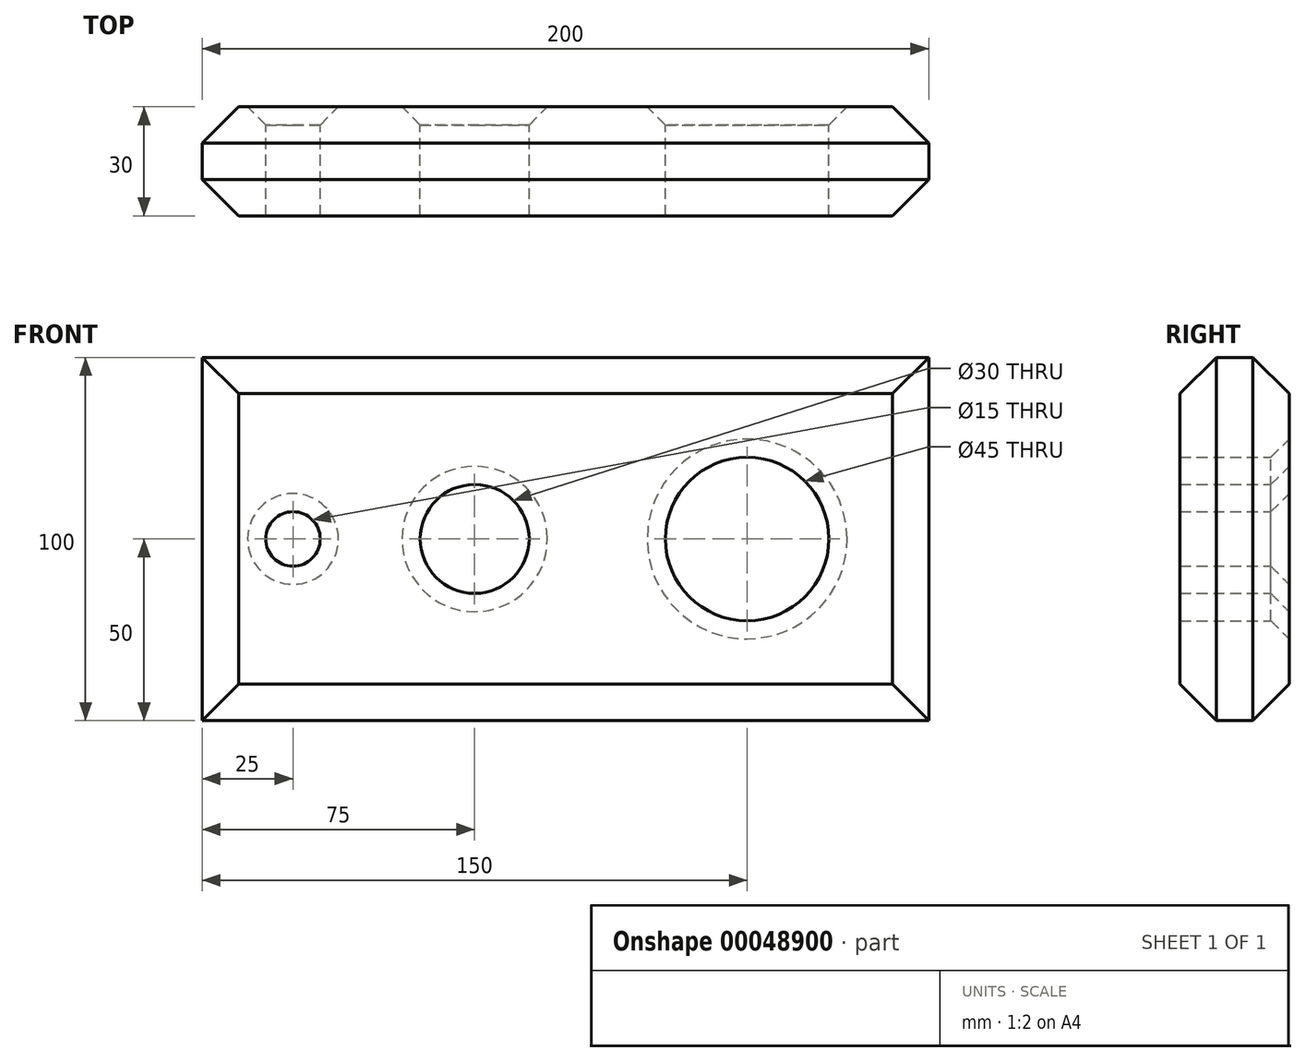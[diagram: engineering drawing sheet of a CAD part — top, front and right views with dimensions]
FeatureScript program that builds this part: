
annotation { "Feature Type Name" : "Feature", "Feature Type Description" : "" }
export const myFeature = defineFeature(function(context is Context, id is Id, definition is map)
    precondition{}
    {
        {
            var Q0;
            Q0=qCreatedBy(makeId("Front.planeOp"),FACE);
            var sketch = newSketch(context, id + "F0", { "sketchPlane" : qUnion([Q0])});
            skLineSegment(sketch, "E0.rect.bottom", {"start": v(100, 50) * mm, "end": v(-100, 50) * mm});
            skLineSegment(sketch, "E0.rect.top", {"start": v(100, -50) * mm, "end": v(-100, -50) * mm});
            skLineSegment(sketch, "E0.rect.left", {"start": v(100, 50) * mm, "end": v(100, -50) * mm});
            skLineSegment(sketch, "E0.rect.right", {"start": v(-100, 50) * mm, "end": v(-100, -50) * mm});
            skPoint(sketch, "E0.rect.middle", {"position": v(0, 0) * mm});
            skLineSegment(sketch, "E1", {"start": v(-75, 50) * mm, "end": v(-75, -50) * mm, "construction": true});
            skLineSegment(sketch, "E2", {"start": v(-25, 50) * mm, "end": v(-25, -50) * mm, "construction": true});
            skLineSegment(sketch, "E3", {"start": v(50, 50) * mm, "end": v(50, -50) * mm, "construction": true});
            skLineSegment(sketch, "E4", {"start": v(-100, 0) * mm, "end": v(100, 0) * mm, "construction": true});
            skCircle(sketch, "E5", {"center": v(-75, 0) * mm, "radius": 7.5 * mm});
            skCircle(sketch, "E6", {"center": v(-25, 0) * mm, "radius": 15 * mm});
            skCircle(sketch, "E7", {"center": v(50, 0) * mm, "radius": 22.5 * mm});
            skSolve(sketch);
        }
        {
            var Q0;
            Q0=makeQuery(id+"F0.imprint","IMPRINT",FACE,{"disambiguationData":[TD([[makeQuery(id+"F0.imprint","IMPRINT",EDGE,{"derivedFrom":sQuery(id+"F0.wireOp",EDGE,"E0.rect.bottom")}),1.0]])]});
            extrude(context, id + "F1", {"entities" : qUnion([Q0]), "depth" : 30 * mm});
        }
        {
            var Q0;
            Q0=makeQuery(id+"F1.opExtrude","CAP_EDGE",EDGE,{"disambiguationData":[OSD([sQuery(id+"F0.wireOp",EDGE,"E5")])],"isStart":true});
            var Q1;
            Q1=makeQuery(id+"F1.opExtrude","CAP_EDGE",EDGE,{"disambiguationData":[OSD([sQuery(id+"F0.wireOp",EDGE,"E6")])],"isStart":true});
            var Q2;
            Q2=makeQuery(id+"F1.opExtrude","CAP_EDGE",EDGE,{"disambiguationData":[OSD([sQuery(id+"F0.wireOp",EDGE,"E7")])],"isStart":true});
            chamfer(context, id + "F2", {"entities" : qUnion([Q0, Q1, Q2]), "chamferType" : ChamferType.OFFSET_ANGLE, "width" : 5 * mm, "oppositeDirection" : false, "angle" : 45 * degree, "tangentPropagation" : true});
        }
        {
            var Q0;
            Q0=makeQuery(id+"F1.opExtrude","CAP_EDGE",EDGE,{"disambiguationData":[OSD([sQuery(id+"F0.wireOp",EDGE,"E0.rect.top")])],"isStart":false});
            var Q1;
            Q1=makeQuery(id+"F1.opExtrude","CAP_EDGE",EDGE,{"disambiguationData":[OSD([sQuery(id+"F0.wireOp",EDGE,"E0.rect.right")])],"isStart":false});
            var Q2;
            Q2=makeQuery(id+"F1.opExtrude","CAP_EDGE",EDGE,{"disambiguationData":[OSD([sQuery(id+"F0.wireOp",EDGE,"E0.rect.bottom")])],"isStart":false});
            var Q3;
            Q3=makeQuery(id+"F1.opExtrude","CAP_EDGE",EDGE,{"disambiguationData":[OSD([sQuery(id+"F0.wireOp",EDGE,"E0.rect.left")])],"isStart":false});
            var Q4;
            Q4=makeQuery(id+"F1.opExtrude","CAP_EDGE",EDGE,{"disambiguationData":[OSD([sQuery(id+"F0.wireOp",EDGE,"E0.rect.left")])],"isStart":true});
            var Q5;
            Q5=makeQuery(id+"F1.opExtrude","CAP_EDGE",EDGE,{"disambiguationData":[OSD([sQuery(id+"F0.wireOp",EDGE,"E0.rect.bottom")])],"isStart":true});
            var Q6;
            Q6=makeQuery(id+"F1.opExtrude","CAP_EDGE",EDGE,{"disambiguationData":[OSD([sQuery(id+"F0.wireOp",EDGE,"E0.rect.right")])],"isStart":true});
            var Q7;
            Q7=makeQuery(id+"F1.opExtrude","CAP_EDGE",EDGE,{"disambiguationData":[OSD([sQuery(id+"F0.wireOp",EDGE,"E0.rect.top")])],"isStart":true});
            chamfer(context, id + "F3", {"entities" : qUnion([Q0, Q1, Q2, Q3, Q4, Q5, Q6, Q7]), "chamferType" : ChamferType.OFFSET_ANGLE, "width" : 10 * mm, "oppositeDirection" : false, "angle" : 45 * degree, "tangentPropagation" : true});
        }
    });
